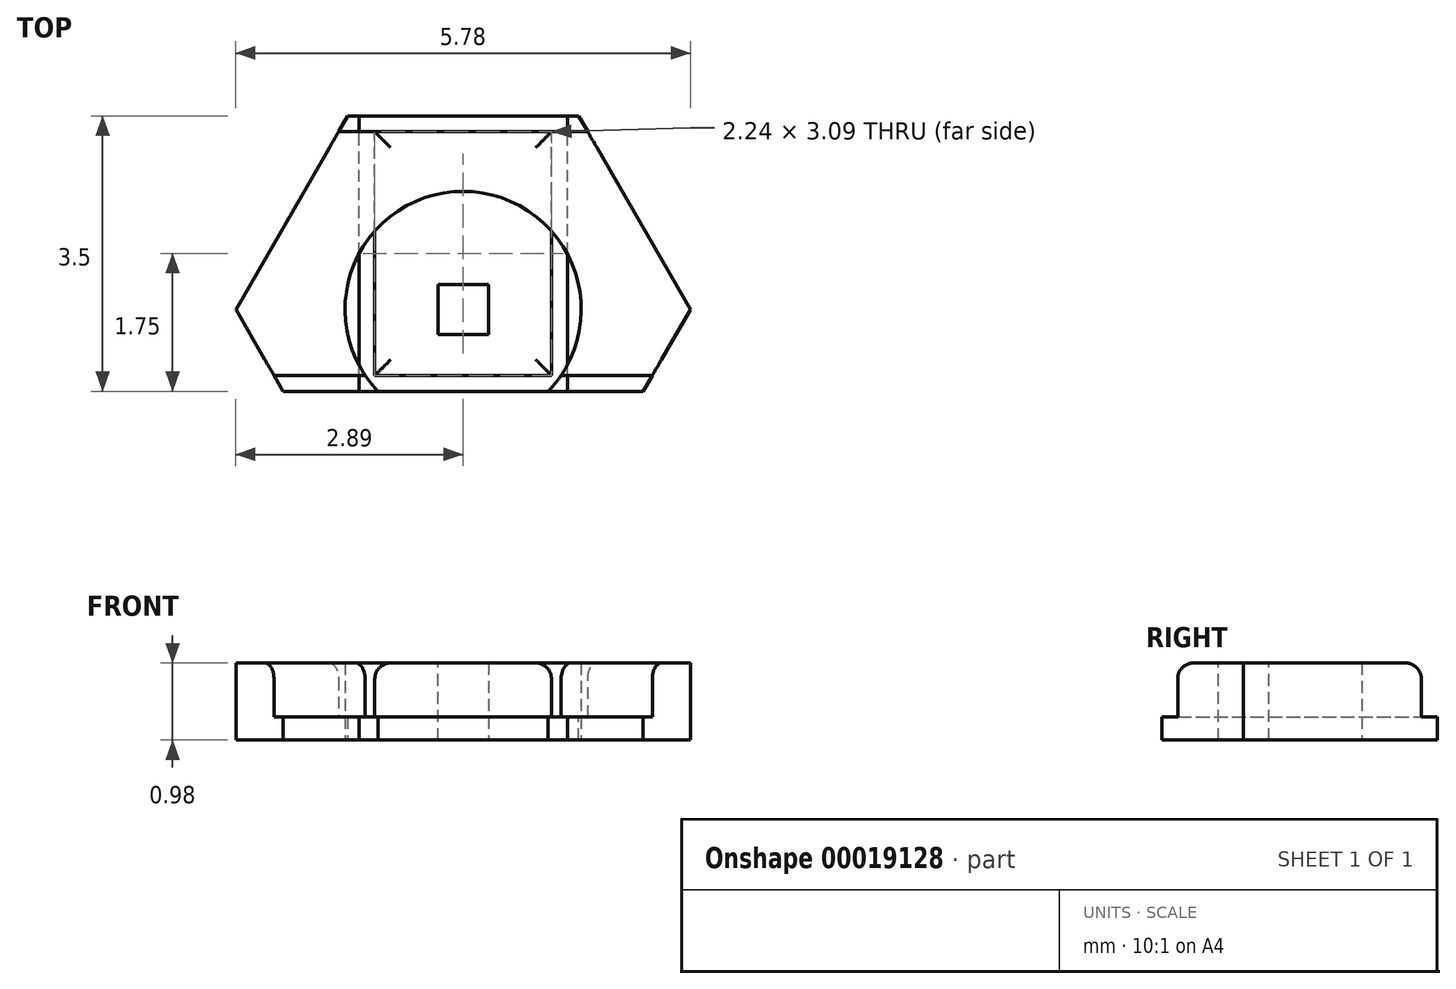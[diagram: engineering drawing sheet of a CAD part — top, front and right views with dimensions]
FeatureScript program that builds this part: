
annotation { "Feature Type Name" : "Feature", "Feature Type Description" : "" }
export const myFeature = defineFeature(function(context is Context, id is Id, definition is map)
    precondition{}
    {
        {
            var Q0;
            Q0=qCreatedBy(makeId("Front.planeOp"),FACE);
            var sketch = newSketch(context, id + "F0", { "sketchPlane" : qUnion([Q0])});
            skLineSegment(sketch, "E0.bottom", {"start": v(-1.12, 0.3) * mm, "end": v(1.12, 0.3) * mm});
            skPoint(sketch, "E1", {"position": v(0, 0.3) * mm});
            skPoint(sketch, "E2.visualSharp", {"position": v(1.12, 0.98) * mm});
            skLineSegment(sketch, "E3.top", {"start": v(-1.32, 0.3) * mm, "end": v(1.32, 0.3) * mm});
            skLineSegment(sketch, "E0.top", {"start": v(-0.92, 0.98) * mm, "end": v(0.92, 0.98) * mm});
            skPoint(sketch, "E4.visualSharp", {"position": v(-1.12, 0.98) * mm});
            skLineSegment(sketch, "E3.bottom", {"start": v(-1.32, 0) * mm, "end": v(1.32, 0) * mm});
            skPoint(sketch, "E5", {"position": v(0, 0) * mm});
            skLineSegment(sketch, "E0.right", {"start": v(1.12, 0.3) * mm, "end": v(1.12, 0.78) * mm});
            skLineSegment(sketch, "E3.left", {"start": v(-1.32, 0) * mm, "end": v(-1.32, 0.3) * mm});
            skLineSegment(sketch, "E0.left", {"start": v(-1.12, 0.3) * mm, "end": v(-1.12, 0.78) * mm});
            skLineSegment(sketch, "E3.right", {"start": v(1.32, 0) * mm, "end": v(1.32, 0.3) * mm});
            skArc(sketch, "E2.filletArc", {"start": v(1.12, 0.78) * mm, "mid": v(1.06, 0.92) * mm, "end": v(0.92, 0.98) * mm});
            skArc(sketch, "E4.filletArc", {"start": v(-0.92, 0.98) * mm, "mid": v(-1.06, 0.92) * mm, "end": v(-1.12, 0.78) * mm});
            skLineSegment(sketch, "E6.bottom", {"start": v(-0.13, 0) * mm, "end": v(0.13, 0) * mm, "construction": true});
            skLineSegment(sketch, "E6.top", {"start": v(-0.12, 0.3) * mm, "end": v(0.12, 0.3) * mm, "construction": true});
            skLineSegment(sketch, "E6.left", {"start": v(-0.13, 0) * mm, "end": v(-0.12, 0.3) * mm, "construction": true});
            skLineSegment(sketch, "E6.right", {"start": v(0.12, 0) * mm, "end": v(0.13, 0.3) * mm, "construction": true});
            skSolve(sketch);
        }
        {
            var Q0;
            Q0=qCreatedBy(makeId("Right.planeOp"),FACE);
            var sketch = newSketch(context, id + "F1", { "sketchPlane" : qUnion([Q0])});
            skLineSegment(sketch, "E7.bottom", {"start": v(-0.84, 0.3) * mm, "end": v(2.26, 0.3) * mm});
            skPoint(sketch, "E8", {"position": v(0, 0.3) * mm});
            skPoint(sketch, "E9.visualSharp", {"position": v(2.26, 0.98) * mm});
            skLineSegment(sketch, "E10.top", {"start": v(-1.04, 0.3) * mm, "end": v(2.46, 0.3) * mm});
            skLineSegment(sketch, "E7.top", {"start": v(-0.64, 0.98) * mm, "end": v(2.06, 0.98) * mm});
            skPoint(sketch, "E11.visualSharp", {"position": v(-0.84, 0.98) * mm});
            skLineSegment(sketch, "E10.bottom", {"start": v(-1.04, 0) * mm, "end": v(2.46, 0) * mm});
            skPoint(sketch, "E12", {"position": v(0, 0) * mm});
            skLineSegment(sketch, "E7.right", {"start": v(2.26, 0.3) * mm, "end": v(2.26, 0.78) * mm});
            skLineSegment(sketch, "E10.left", {"start": v(-1.04, 0) * mm, "end": v(-1.04, 0.3) * mm});
            skLineSegment(sketch, "E7.left", {"start": v(-0.84, 0.3) * mm, "end": v(-0.84, 0.78) * mm});
            skLineSegment(sketch, "E10.right", {"start": v(2.46, 0) * mm, "end": v(2.46, 0.3) * mm});
            skArc(sketch, "E9.filletArc", {"start": v(2.26, 0.78) * mm, "mid": v(2.2, 0.92) * mm, "end": v(2.06, 0.98) * mm});
            skArc(sketch, "E11.filletArc", {"start": v(-0.64, 0.98) * mm, "mid": v(-0.78, 0.92) * mm, "end": v(-0.84, 0.78) * mm});
            skLineSegment(sketch, "E13.bottom", {"start": v(-0.12, 0) * mm, "end": v(0.12, 0) * mm, "construction": true});
            skLineSegment(sketch, "E13.top", {"start": v(-0.12, 0.3) * mm, "end": v(0.13, 0.3) * mm, "construction": true});
            skLineSegment(sketch, "E13.left", {"start": v(-0.12, 0) * mm, "end": v(-0.12, 0.3) * mm, "construction": true});
            skLineSegment(sketch, "E13.right", {"start": v(0.13, 0) * mm, "end": v(0.13, 0.3) * mm, "construction": true});
            skPoint(sketch, "E14", {"position": v(0.71, 0.3) * mm});
            skPoint(sketch, "E15", {"position": v(0.7, 0.98) * mm});
            skSolve(sketch);
        }
        {
            var Q0;
            Q0=qCreatedBy(makeId("Top.planeOp"),FACE);
            var sketch = newSketch(context, id + "F2", { "sketchPlane" : qUnion([Q0])});
            skCircle(sketch, "E16.cCircle", {"center": v(0, 0) * mm, "radius": 2.5 * mm, "construction": true});
            skLineSegment(sketch, "E16.0", {"start": v(2.89, 0) * mm, "end": v(1.44, -2.5) * mm});
            skLineSegment(sketch, "E16.1", {"start": v(1.44, -2.5) * mm, "end": v(-1.44, -2.5) * mm});
            skLineSegment(sketch, "E16.2", {"start": v(-1.44, -2.5) * mm, "end": v(-2.89, 0) * mm});
            skLineSegment(sketch, "E16.3", {"start": v(-2.89, 0) * mm, "end": v(-1.44, 2.5) * mm});
            skLineSegment(sketch, "E16.4", {"start": v(-1.44, 2.5) * mm, "end": v(1.44, 2.5) * mm});
            skLineSegment(sketch, "E16.5", {"start": v(1.44, 2.5) * mm, "end": v(2.89, 0) * mm});
            skPoint(sketch, "E16.0.midPoint", {"position": v(2.17, -1.25) * mm});
            skCircle(sketch, "E17", {"center": v(0, 0) * mm, "radius": 1.5 * mm});
            skSolve(sketch);
        }
        {
            var Q0;
            Q0=makeQuery(id+"F0.imprint","IMPRINT",FACE,{"disambiguationData":[TD([[makeQuery(id+"F0.imprint","IMPRINT",EDGE,{"derivedFrom":sQuery(id+"F0.wireOp",EDGE,"E3.bottom")}),1.0]])]});
            var Q1;
            Q1=makeQuery(id+"F0.imprint","IMPRINT",FACE,{"disambiguationData":[TD([[makeQuery(id+"F0.imprint","IMPRINT",EDGE,{"derivedFrom":sQuery(id+"F0.wireOp",EDGE,"E0.top")}),-1.0]])]});
            extrude(context, id + "F3", {"entities" : qUnion([Q0, Q1]), "depth" : 1.04 * mm, "hasSecondDirection" : true, "secondDirectionOppositeDirection" : true, "secondDirectionDepth" : 2.46 * mm});
        }
        {
            var Q0;
            Q0=makeQuery(id+"F2.imprint","IMPRINT",FACE,{"disambiguationData":[TD([[makeQuery(id+"F2.imprint","IMPRINT",EDGE,{"derivedFrom":sQuery(id+"F2.wireOp",EDGE,"E16.0")}),-1.0]])]});
            extrude(context, id + "F4", {"entities" : qUnion([Q0]), "depth" : 12 * mm});
        }
        {
            var Q0;
            Q0=makeQuery(id+"F3.opExtrude","SWEPT_BODY",BODY,{"disambiguationData":[OSD([sQuery(id+"F0.wireOp",EDGE,"E3.top"),sQuery(id+"F0.wireOp",EDGE,"E0.top"),sQuery(id+"F0.wireOp",EDGE,"E3.bottom"),sQuery(id+"F0.wireOp",EDGE,"E0.right"),sQuery(id+"F0.wireOp",EDGE,"E3.left"),sQuery(id+"F0.wireOp",EDGE,"E0.left"),sQuery(id+"F0.wireOp",EDGE,"E3.right"),sQuery(id+"F0.wireOp",EDGE,"E2.filletArc"),sQuery(id+"F0.wireOp",EDGE,"E4.filletArc")])]});
            transform(context, id + "F5", {"entities" : qUnion([Q0]), "transformType" : TransformType.TRANSLATION_3D, "dx" : 0 * mm, "dy" : 0 * mm, "dz" : 0 * mm, "makeCopy" : true});
        }
        {
            var Q0;
            Q0=qCreatedBy(makeId("Front.planeOp"),FACE);
            var sketch = newSketch(context, id + "F6", { "sketchPlane" : qUnion([Q0])});
            skLineSegment(sketch, "E18", {"start": v(0, 16.62) * mm, "end": v(0, -15.98) * mm, "construction": true});
            skLineSegment(sketch, "E19", {"start": v(-5.67, 0) * mm, "end": v(6.16, 0) * mm, "construction": true});
            skLineSegment(sketch, "E20", {"start": v(-0.32, 0) * mm, "end": v(-0.32, 18.16) * mm});
            skLineSegment(sketch, "E21.MirrorCS", {"start": v(0.32, 0) * mm, "end": v(0.32, 18.16) * mm});
            skLineSegment(sketch, "E22.MirrorCS", {"start": v(-0.32, 0) * mm, "end": v(-0.32, -18.16) * mm});
            skLineSegment(sketch, "E23.MirrorCS", {"start": v(0.32, 0) * mm, "end": v(0.32, -18.16) * mm});
            skLineSegment(sketch, "E24", {"start": v(0, 12.82) * mm, "end": v(-1.27, 12.82) * mm});
            skLineSegment(sketch, "E25", {"start": v(-1.27, 12.82) * mm, "end": v(-1.27, 15.1) * mm});
            skLineSegment(sketch, "E26", {"start": v(-1.27, 15.1) * mm, "end": v(0, 15.1) * mm});
            skLineSegment(sketch, "E27.MirrorCS", {"start": v(1.27, 15.1) * mm, "end": v(0, 15.1) * mm});
            skLineSegment(sketch, "E28.MirrorCS", {"start": v(1.27, 12.82) * mm, "end": v(1.27, 15.1) * mm});
            skLineSegment(sketch, "E29.MirrorCS", {"start": v(0, 12.82) * mm, "end": v(1.27, 12.82) * mm});
            skLineSegment(sketch, "E30", {"start": v(0, -13.08) * mm, "end": v(-1.27, -13.08) * mm});
            skLineSegment(sketch, "E31", {"start": v(-1.27, -13.08) * mm, "end": v(-1.27, -15.37) * mm});
            skLineSegment(sketch, "E32", {"start": v(-1.27, -15.37) * mm, "end": v(0, -15.37) * mm});
            skLineSegment(sketch, "E33.MirrorCS", {"start": v(1.27, -13.08) * mm, "end": v(1.27, -15.37) * mm});
            skLineSegment(sketch, "E34.MirrorCS", {"start": v(0, -13.08) * mm, "end": v(1.27, -13.08) * mm});
            skLineSegment(sketch, "E35.MirrorCS", {"start": v(1.27, -15.37) * mm, "end": v(0, -15.37) * mm});
            skLineSegment(sketch, "E36", {"start": v(-0.32, 18.16) * mm, "end": v(0.32, 18.16) * mm});
            skLineSegment(sketch, "E37.MirrorCS", {"start": v(-0.32, -18.16) * mm, "end": v(0.32, -18.16) * mm});
            skSolve(sketch);
        }
        {
            var Q0;
            {var subQ5=sQuery(id+"F6.wireOp",EDGE,"E22.MirrorCS");var subQ12=sQuery(id+"F6.wireOp",EDGE,"E20");var subQ14=makeQuery(id+"F6.imprint","INTERSECT",VERTEX,{"derivedFrom":[subQ12,subQ5]});Q0=makeQuery(id+"F6.imprint","IMPRINT",FACE,{"disambiguationData":[TD([[makeQuery(id+"F6.imprint","IMPRINT",EDGE,{"disambiguationData":[TD([[subQ14,-1.0]])],"derivedFrom":subQ12}),-1.0]])]});}
            var Q1;
            {var subQ0=sQuery(id+"F6.wireOp",EDGE,"E34.MirrorCS");var subQ1=sQuery(id+"F6.wireOp",EDGE,"E23.MirrorCS");var subQ2=makeQuery(id+"F6.imprint","INTERSECT",VERTEX,{"derivedFrom":[subQ1,subQ0]});Q1=makeQuery(id+"F6.imprint","IMPRINT",FACE,{"disambiguationData":[TD([[makeQuery(id+"F6.imprint","IMPRINT",EDGE,{"disambiguationData":[TD([[subQ2,-1.0]])],"derivedFrom":subQ1}),-1.0]])]});}
            var Q2;
            {var subQ0=sQuery(id+"F6.wireOp",EDGE,"E37.MirrorCS");Q2=makeQuery(id+"F6.imprint","IMPRINT",FACE,{"disambiguationData":[TD([[makeQuery(id+"F6.imprint","IMPRINT",EDGE,{"derivedFrom":subQ0}),1.0]])]});}
            var Q3;
            {var subQ3=sQuery(id+"F6.wireOp",EDGE,"E24");var subQ9=sQuery(id+"F6.wireOp",EDGE,"E20");var subQ11=makeQuery(id+"F6.imprint","INTERSECT",VERTEX,{"derivedFrom":[subQ9,subQ3]});Q3=makeQuery(id+"F6.imprint","IMPRINT",FACE,{"disambiguationData":[TD([[makeQuery(id+"F6.imprint","IMPRINT",EDGE,{"disambiguationData":[TD([[subQ11,-1.0]])],"derivedFrom":subQ9}),-1.0]])]});}
            var Q4;
            {var subQ0=sQuery(id+"F6.wireOp",EDGE,"E36");Q4=makeQuery(id+"F6.imprint","IMPRINT",FACE,{"disambiguationData":[TD([[makeQuery(id+"F6.imprint","IMPRINT",EDGE,{"derivedFrom":subQ0}),-1.0]])]});}
            extrude(context, id + "F7", {"entities" : qUnion([Q0, Q1, Q2, Q3, Q4]), "depth" : .64 * mm, "symmetric" : true});
        }
        {
            var Q0;
            Q0=makeQuery(id+"F7.opExtrude","CAP_EDGE",EDGE,{"disambiguationData":[OSD([sQuery(id+"F6.wireOp",EDGE,"E36")])],"isStart":false});
            var Q1;
            Q1=makeQuery(id+"F7.opExtrude","CAP_EDGE",EDGE,{"disambiguationData":[OSD([sQuery(id+"F6.wireOp",EDGE,"E36")])],"isStart":true});
            var Q2;
            Q2=makeQuery(id+"F7.opExtrude","SWEPT_EDGE",EDGE,{"disambiguationData":[OSD([sQuery(id+"F6.wireOp",EDGE,"E20"),sQuery(id+"F6.wireOp",EDGE,"E36")])]});
            var Q3;
            Q3=makeQuery(id+"F7.opExtrude","SWEPT_EDGE",EDGE,{"disambiguationData":[OSD([sQuery(id+"F6.wireOp",EDGE,"E21.MirrorCS"),sQuery(id+"F6.wireOp",EDGE,"E36")])]});
            var Q4;
            Q4=makeQuery(id+"F7.opExtrude","CAP_EDGE",EDGE,{"disambiguationData":[OSD([sQuery(id+"F6.wireOp",EDGE,"E37.MirrorCS")])],"isStart":false});
            var Q5;
            Q5=makeQuery(id+"F7.opExtrude","SWEPT_EDGE",EDGE,{"disambiguationData":[OSD([sQuery(id+"F6.wireOp",EDGE,"E22.MirrorCS"),sQuery(id+"F6.wireOp",EDGE,"E37.MirrorCS")])]});
            var Q6;
            Q6=makeQuery(id+"F7.opExtrude","SWEPT_EDGE",EDGE,{"disambiguationData":[OSD([sQuery(id+"F6.wireOp",EDGE,"E23.MirrorCS"),sQuery(id+"F6.wireOp",EDGE,"E37.MirrorCS")])]});
            var Q7;
            Q7=makeQuery(id+"F7.opExtrude","CAP_EDGE",EDGE,{"disambiguationData":[OSD([sQuery(id+"F6.wireOp",EDGE,"E37.MirrorCS")])],"isStart":true});
            chamfer(context, id + "F8", {"entities" : qUnion([Q0, Q1, Q2, Q3, Q4, Q5, Q6, Q7]), "width" : .2 * mm, "tangentPropagation" : true});
        }
        {
            var Q0;
            {var subQ3=sQuery(id+"F6.wireOp",EDGE,"E25");Q0=makeQuery(id+"F6.imprint","IMPRINT",FACE,{"disambiguationData":[TD([[makeQuery(id+"F6.imprint","IMPRINT",EDGE,{"derivedFrom":subQ3}),-1.0]])]});}
            var Q1;
            {var subQ3=sQuery(id+"F6.wireOp",EDGE,"E28.MirrorCS");Q1=makeQuery(id+"F6.imprint","IMPRINT",FACE,{"disambiguationData":[TD([[makeQuery(id+"F6.imprint","IMPRINT",EDGE,{"derivedFrom":subQ3}),1.0]])]});}
            var Q2;
            {var subQ3=sQuery(id+"F6.wireOp",EDGE,"E24");var subQ9=sQuery(id+"F6.wireOp",EDGE,"E20");var subQ11=makeQuery(id+"F6.imprint","INTERSECT",VERTEX,{"derivedFrom":[subQ9,subQ3]});Q2=makeQuery(id+"F6.imprint","IMPRINT",FACE,{"disambiguationData":[TD([[makeQuery(id+"F6.imprint","IMPRINT",EDGE,{"disambiguationData":[TD([[subQ11,-1.0]])],"derivedFrom":subQ9}),-1.0]])]});}
            var Q3;
            {var subQ0=sQuery(id+"F6.wireOp",EDGE,"E31");Q3=makeQuery(id+"F6.imprint","IMPRINT",FACE,{"disambiguationData":[TD([[makeQuery(id+"F6.imprint","IMPRINT",EDGE,{"derivedFrom":subQ0}),1.0]])]});}
            var Q4;
            {var subQ0=sQuery(id+"F6.wireOp",EDGE,"E34.MirrorCS");var subQ1=sQuery(id+"F6.wireOp",EDGE,"E23.MirrorCS");var subQ2=makeQuery(id+"F6.imprint","INTERSECT",VERTEX,{"derivedFrom":[subQ1,subQ0]});Q4=makeQuery(id+"F6.imprint","IMPRINT",FACE,{"disambiguationData":[TD([[makeQuery(id+"F6.imprint","IMPRINT",EDGE,{"disambiguationData":[TD([[subQ2,-1.0]])],"derivedFrom":subQ1}),-1.0]])]});}
            var Q5;
            {var subQ3=sQuery(id+"F6.wireOp",EDGE,"E33.MirrorCS");Q5=makeQuery(id+"F6.imprint","IMPRINT",FACE,{"disambiguationData":[TD([[makeQuery(id+"F6.imprint","IMPRINT",EDGE,{"derivedFrom":subQ3}),-1.0]])]});}
            extrude(context, id + "F9", {"entities" : qUnion([Q0, Q1, Q2, Q3, Q4, Q5]), "depth" : 2.34 * mm, "symmetric" : true});
        }
        {
            var Q0;
            Q0=makeQuery(id+"F9.opExtrude","CAP_EDGE",EDGE,{"disambiguationData":[OSD([sQuery(id+"F6.wireOp",EDGE,"E25")])],"isStart":true});
            var Q1;
            Q1=makeQuery(id+"F9.opExtrude","CAP_EDGE",EDGE,{"disambiguationData":[OSD([sQuery(id+"F6.wireOp",EDGE,"E28.MirrorCS")])],"isStart":true});
            var Q2;
            Q2=makeQuery(id+"F9.opExtrude","CAP_EDGE",EDGE,{"disambiguationData":[OSD([sQuery(id+"F6.wireOp",EDGE,"E25")])],"isStart":false});
            var Q3;
            Q3=makeQuery(id+"F9.opExtrude","CAP_EDGE",EDGE,{"disambiguationData":[OSD([sQuery(id+"F6.wireOp",EDGE,"E28.MirrorCS")])],"isStart":false});
            var Q4;
            Q4=makeQuery(id+"F9.opExtrude","CAP_EDGE",EDGE,{"disambiguationData":[OSD([sQuery(id+"F6.wireOp",EDGE,"E33.MirrorCS")])],"isStart":false});
            var Q5;
            Q5=makeQuery(id+"F9.opExtrude","CAP_EDGE",EDGE,{"disambiguationData":[OSD([sQuery(id+"F6.wireOp",EDGE,"E31")])],"isStart":true});
            var Q6;
            Q6=makeQuery(id+"F9.opExtrude","CAP_EDGE",EDGE,{"disambiguationData":[OSD([sQuery(id+"F6.wireOp",EDGE,"E33.MirrorCS")])],"isStart":true});
            var Q7;
            Q7=makeQuery(id+"F9.opExtrude","CAP_EDGE",EDGE,{"disambiguationData":[OSD([sQuery(id+"F6.wireOp",EDGE,"E31")])],"isStart":false});
            chamfer(context, id + "F10", {"entities" : qUnion([Q0, Q1, Q2, Q3, Q4, Q5, Q6, Q7]), "width" : .2 * mm, "tangentPropagation" : true});
        }
        {
            var Q0;
            Q0 = qSketchRegion(id + "F1", true);
            extrude(context, id + "F11", {"entities" : qUnion([Q0]), "operationType" : NewBodyOperationType.INTERSECT, "oppositeDirection" : true, "depth" : 25 * mm, "symmetric" : true});
        }
    });
